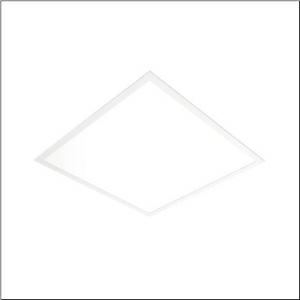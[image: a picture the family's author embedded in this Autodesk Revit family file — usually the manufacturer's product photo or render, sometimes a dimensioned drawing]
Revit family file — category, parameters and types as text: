
# Revit family: apollon_r__41_51mh11wm2443_3aa7
name_source: partatom
category: Lighting Fixtures
units: mm (PartAtom-declared; Revit-internal decimal feet)

## family parameters
Cut with Voids When Loaded = No
Host = Face
Light Source = No
Part Type = Normal
Room Calculation Point = No
Round Connector Dimension = Use Diameter
Shared = No

## types (1)
- --- (1 x LED, 4380 lm, 35 W, 4000K)
    Apparent Load = 35 VA
    CIE Flux Codes = 61 87 97 100 100
    Color Rendering = 80
    Color Temperature = 4000K
    Default Elevation = 1800 mm
    Description = Apollon® 41, office luminaire, primary optical cover: prismatic diffuser, of PS, light emission: direct distribution, primary light characteristic: symmetric, installation type: lay-in mounting, LED, rated luminous flux: 4.375lm, luminous efficacy: 125lm/W, light colour: 840, colour temperature: 4000K, control gear: ON/OFF Multilumen, with terminal, 3-pole, mains connection: 220..240V, AC, 50/60Hz, rated input power: 35W, housing, of aluminium section, traffic white (RAL 9016), module: M625, length: 620mm, width: 620mm, height: 60mm, recess depth: 180mm, housing upper side, of sheet steel, protection rating (complete): IP20, protection rating (lamp compartment, on room side): IP40, insulation class (complete): insulation class II (safety insulation), certification: CE, ENEC, impact resistance: IK03, permissible operating ambient temperature: -25..+40°C, packaging unit: 1 piece
    Height = 0 mm  [stored 0 ft]
    Lamp = 1 x LED
    Lamp Light Flux = 4380 lm
    Lamp Power = 35 W
    Lamp count = 1
    Length = 620 mm
    Luminous efficacy = 125 lm/W
    Manufacturer = Siteco
    ModVariant = No
    Model = 51MH11WM2443
    Mounting Place = Ceiling
    Mounting Type = Recessed
    Number of Poles = 1
    OnlyDefault = Yes
    Power Factor = 1
    Product Name = Apollon® 41
    Product group = office luminaire | ceiling recessed
    ProductGroupID = 401
    Protection Class = Protection class II
    Protection Degree = IP 20
    RLX_Detail_Level = 1
    RLX_Emergency_Light_Flux = 0 lm
    RLX_Emergency_Type = 0
    RLX_Emergency_Type_DB = No
    RlxData = <blob elided: 12981 chars, md5=d93a2d4f>
    Socket = socket
    Standby Power = 0 W
    System Light Flux = 4380 lm
    System Power = 35 W
    Type Comments = factory setting: luminous flux: 100 % | (ON | ON) | 900 mA
    Type Image = l_1291024.jpg
    URL = http://relux.com
    VarID = @adj_013663
    Voltage = 0 V
    Weight = 0.00 kg
    Width = 620 mm

note: [stored X ft] marks values corroborated as IEEE doubles in the binary element streams (Revit-internal decimal feet)

## geometry (parser evidence)
native form markers: Sweep x8
no freeform markers — native parametric forms only
